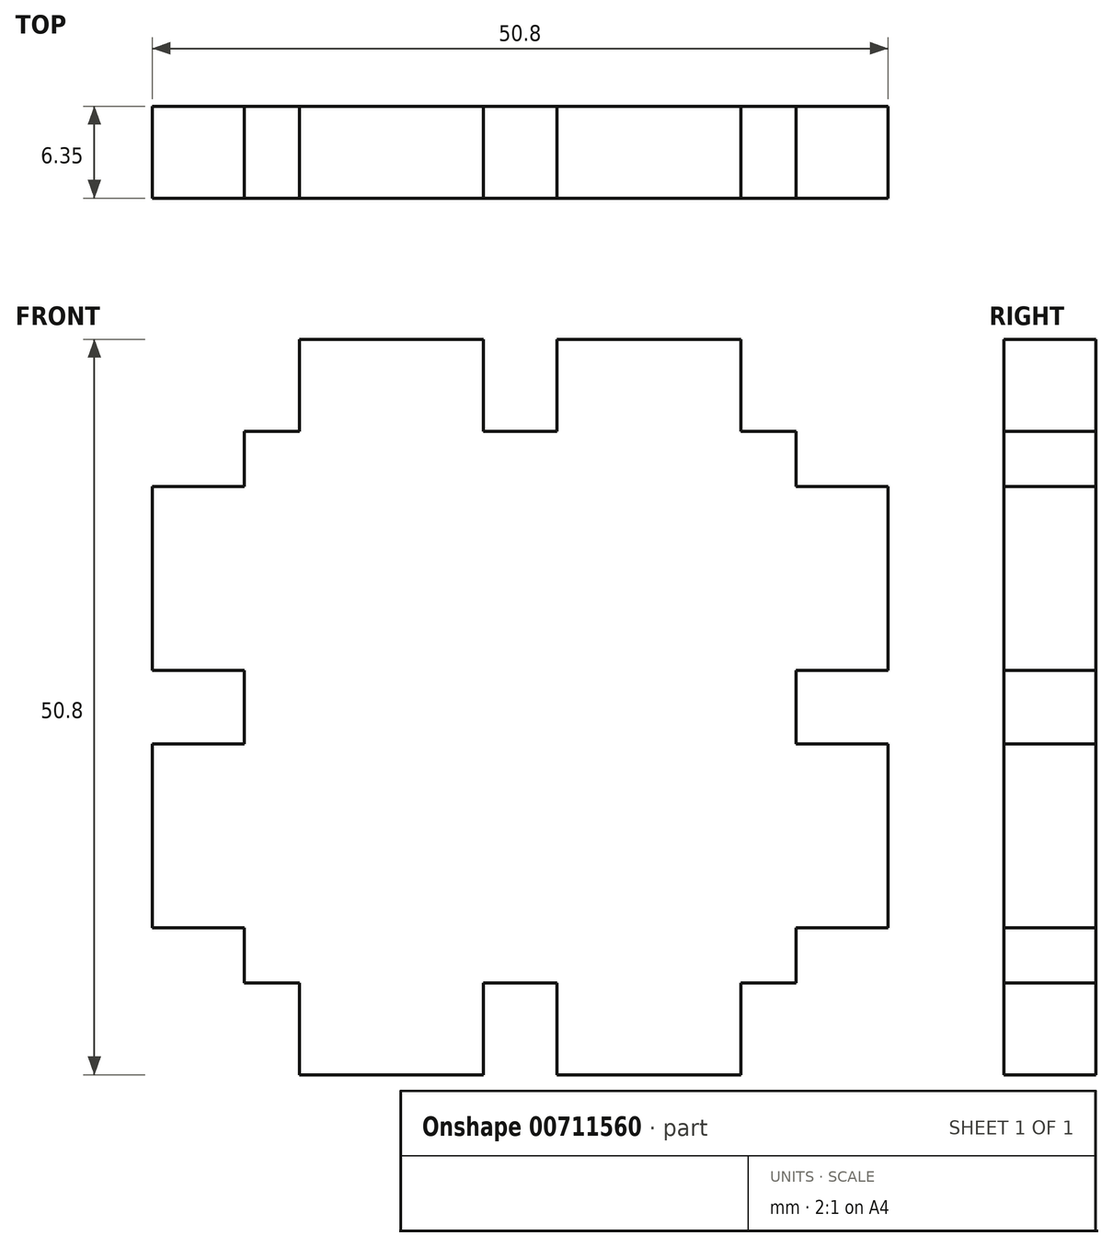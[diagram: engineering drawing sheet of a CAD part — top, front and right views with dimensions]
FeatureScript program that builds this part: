
annotation { "Feature Type Name" : "Feature", "Feature Type Description" : "" }
export const myFeature = defineFeature(function(context is Context, id is Id, definition is map)
    precondition{}
    {
        {
            var Q0;
            Q0=qCreatedBy(makeId("Front.planeOp"),FACE);
            var sketch = newSketch(context, id + "F0", { "sketchPlane" : qUnion([Q0])});
            skLineSegment(sketch, "E0.bottom", {"start": v(25.4, 25.4) * mm, "end": v(-25.4, 25.4) * mm, "construction": true});
            skLineSegment(sketch, "E0.top", {"start": v(25.4, -25.4) * mm, "end": v(-25.4, -25.4) * mm, "construction": true});
            skLineSegment(sketch, "E0.left", {"start": v(25.4, 25.4) * mm, "end": v(25.4, -25.4) * mm, "construction": true});
            skLineSegment(sketch, "E0.right", {"start": v(-25.4, 25.4) * mm, "end": v(-25.4, -25.4) * mm, "construction": true});
            skPoint(sketch, "E0.middle", {"position": v(0, 0) * mm});
            skLineSegment(sketch, "E1", {"start": v(-19.05, 25.4) * mm, "end": v(-19.05, -25.4) * mm, "construction": true});
            skLineSegment(sketch, "E2", {"start": v(-2.54, -25.4) * mm, "end": v(-2.54, 25.4) * mm, "construction": true});
            skLineSegment(sketch, "E3", {"start": v(2.54, 25.4) * mm, "end": v(2.54, -25.4) * mm, "construction": true});
            skLineSegment(sketch, "E4", {"start": v(15.24, 25.4) * mm, "end": v(15.24, -25.4) * mm, "construction": true});
            skLineSegment(sketch, "E5", {"start": v(-15.24, 25.4) * mm, "end": v(-15.24, -25.4) * mm, "construction": true});
            skLineSegment(sketch, "E6", {"start": v(19.05, 25.4) * mm, "end": v(19.05, -25.4) * mm, "construction": true});
            skLineSegment(sketch, "E7", {"start": v(-25.4, 19.05) * mm, "end": v(25.4, 19.05) * mm, "construction": true});
            skLineSegment(sketch, "E8", {"start": v(-25.4, 15.24) * mm, "end": v(25.4, 15.24) * mm, "construction": true});
            skLineSegment(sketch, "E9", {"start": v(-25.4, 2.54) * mm, "end": v(25.4, 2.54) * mm, "construction": true});
            skLineSegment(sketch, "E10", {"start": v(-25.4, -19.05) * mm, "end": v(25.4, -19.05) * mm, "construction": true});
            skLineSegment(sketch, "E11", {"start": v(-25.4, -15.24) * mm, "end": v(25.4, -15.24) * mm, "construction": true});
            skLineSegment(sketch, "E12", {"start": v(-25.4, -2.54) * mm, "end": v(25.4, -2.54) * mm, "construction": true});
            skLineSegment(sketch, "E13", {"start": v(-25.4, 15.24) * mm, "end": v(-25.4, 2.54) * mm});
            skLineSegment(sketch, "E14", {"start": v(-25.4, 2.54) * mm, "end": v(-19.05, 2.54) * mm});
            skLineSegment(sketch, "E15", {"start": v(-19.05, 2.54) * mm, "end": v(-19.05, -2.54) * mm});
            skLineSegment(sketch, "E16", {"start": v(-19.05, -2.54) * mm, "end": v(-25.4, -2.54) * mm});
            skLineSegment(sketch, "E17", {"start": v(-25.4, -2.54) * mm, "end": v(-25.4, -15.24) * mm});
            skLineSegment(sketch, "E18", {"start": v(-25.4, -15.24) * mm, "end": v(-19.05, -15.24) * mm});
            skLineSegment(sketch, "E19", {"start": v(-19.05, -15.24) * mm, "end": v(-19.05, -19.05) * mm});
            skLineSegment(sketch, "E20", {"start": v(-19.05, -19.05) * mm, "end": v(-15.24, -19.05) * mm});
            skLineSegment(sketch, "E21", {"start": v(-15.24, -19.05) * mm, "end": v(-15.24, -25.4) * mm});
            skLineSegment(sketch, "E22", {"start": v(-15.24, -25.4) * mm, "end": v(-2.54, -25.4) * mm});
            skLineSegment(sketch, "E23", {"start": v(-2.54, -25.4) * mm, "end": v(-2.54, -19.05) * mm});
            skLineSegment(sketch, "E24", {"start": v(-2.54, -19.05) * mm, "end": v(2.54, -19.05) * mm});
            skLineSegment(sketch, "E25", {"start": v(2.54, -19.05) * mm, "end": v(2.54, -25.4) * mm});
            skLineSegment(sketch, "E26", {"start": v(2.54, -25.4) * mm, "end": v(15.24, -25.4) * mm});
            skLineSegment(sketch, "E27", {"start": v(15.24, -25.4) * mm, "end": v(15.24, -19.05) * mm});
            skLineSegment(sketch, "E28", {"start": v(15.24, -19.05) * mm, "end": v(19.05, -19.05) * mm});
            skLineSegment(sketch, "E29", {"start": v(19.05, -19.05) * mm, "end": v(19.05, -15.24) * mm});
            skLineSegment(sketch, "E30", {"start": v(19.05, -15.24) * mm, "end": v(25.4, -15.24) * mm});
            skLineSegment(sketch, "E31", {"start": v(25.4, -15.24) * mm, "end": v(25.4, -2.54) * mm});
            skLineSegment(sketch, "E32", {"start": v(25.4, -2.54) * mm, "end": v(19.05, -2.54) * mm});
            skLineSegment(sketch, "E33", {"start": v(19.05, -2.54) * mm, "end": v(19.05, 2.54) * mm});
            skLineSegment(sketch, "E34", {"start": v(19.05, 2.54) * mm, "end": v(25.4, 2.54) * mm});
            skLineSegment(sketch, "E35", {"start": v(25.4, 2.54) * mm, "end": v(25.4, 15.24) * mm});
            skLineSegment(sketch, "E36", {"start": v(25.4, 15.24) * mm, "end": v(19.05, 15.24) * mm});
            skLineSegment(sketch, "E37", {"start": v(19.05, 15.24) * mm, "end": v(19.05, 19.05) * mm});
            skLineSegment(sketch, "E38", {"start": v(19.05, 19.05) * mm, "end": v(15.24, 19.05) * mm});
            skLineSegment(sketch, "E39", {"start": v(15.24, 19.05) * mm, "end": v(15.24, 25.4) * mm});
            skLineSegment(sketch, "E40", {"start": v(15.24, 25.4) * mm, "end": v(2.54, 25.4) * mm});
            skLineSegment(sketch, "E41", {"start": v(2.54, 25.4) * mm, "end": v(2.54, 19.05) * mm});
            skLineSegment(sketch, "E42", {"start": v(2.54, 19.05) * mm, "end": v(-2.54, 19.05) * mm});
            skLineSegment(sketch, "E43", {"start": v(-2.54, 19.05) * mm, "end": v(-2.54, 25.4) * mm});
            skLineSegment(sketch, "E44", {"start": v(-2.54, 25.4) * mm, "end": v(-15.24, 25.4) * mm});
            skLineSegment(sketch, "E45", {"start": v(-15.24, 25.4) * mm, "end": v(-15.24, 19.05) * mm});
            skLineSegment(sketch, "E46", {"start": v(-15.24, 19.05) * mm, "end": v(-19.05, 19.05) * mm});
            skLineSegment(sketch, "E47", {"start": v(-19.05, 19.05) * mm, "end": v(-19.05, 15.24) * mm});
            skLineSegment(sketch, "E48", {"start": v(-19.05, 15.24) * mm, "end": v(-25.4, 15.24) * mm});
            skSolve(sketch);
        }
        {
            var Q0;
            Q0=makeQuery(id+"F0.imprint","IMPRINT",FACE,{"disambiguationData":[TD([[makeQuery(id+"F0.imprint","IMPRINT",EDGE,{"derivedFrom":sQuery(id+"F0.wireOp",EDGE,"E13")}),1.0]])]});
            extrude(context, id + "F1", {"entities" : qUnion([Q0]), "depth" : 6.35 * mm, "offsetDistance" : 25.4 * mm});
        }
    });
